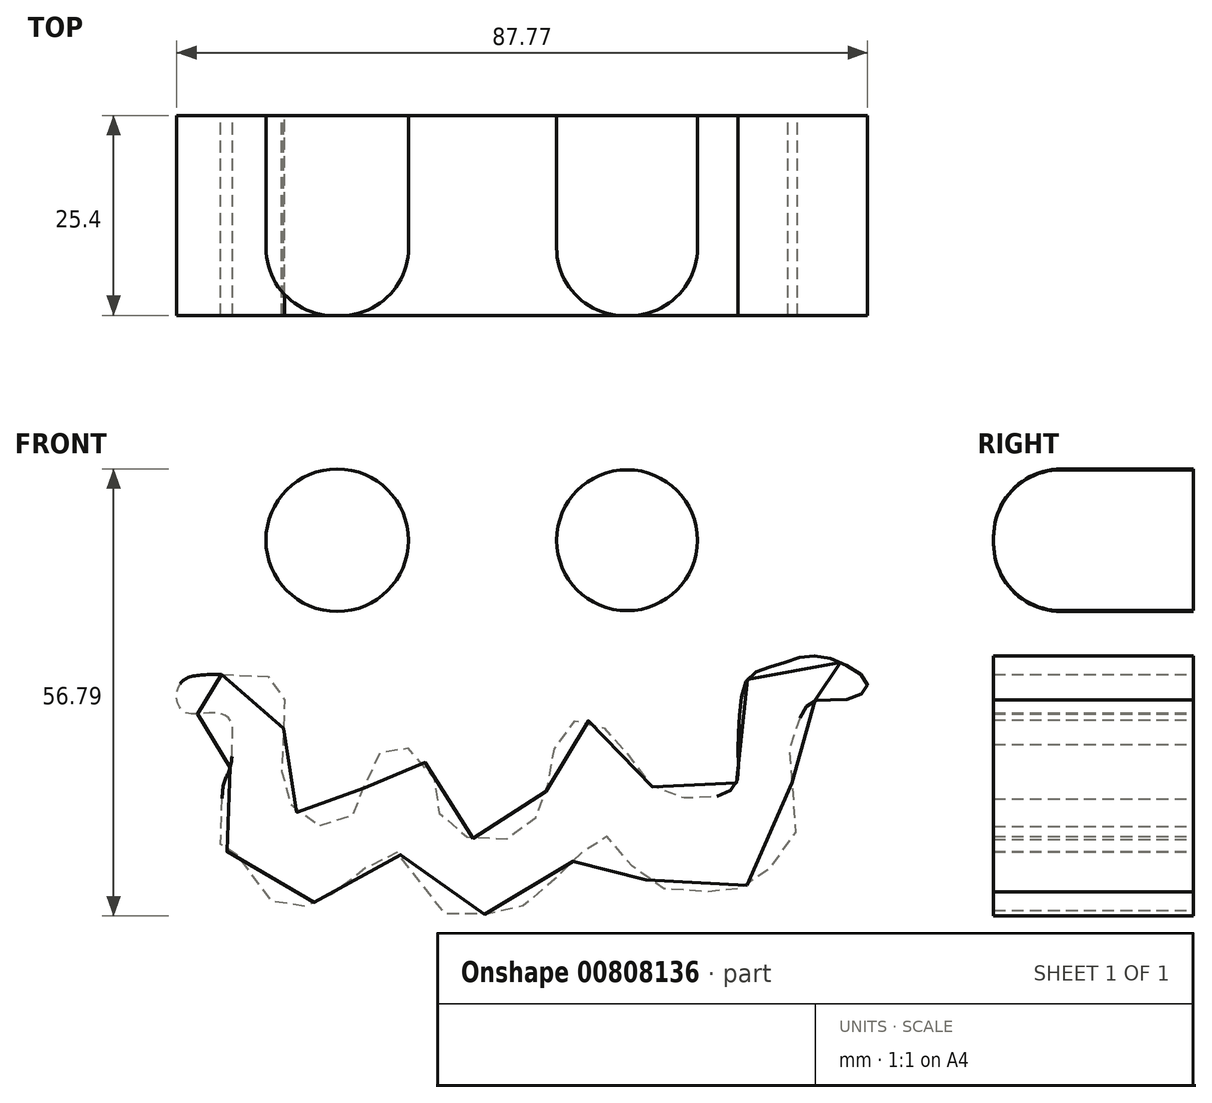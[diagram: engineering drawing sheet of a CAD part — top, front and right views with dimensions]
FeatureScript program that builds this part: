
annotation { "Feature Type Name" : "Feature", "Feature Type Description" : "" }
export const myFeature = defineFeature(function(context is Context, id is Id, definition is map)
    precondition{}
    {
        {
            var Q0;
            Q0=qCreatedBy(makeId("Front.planeOp"),FACE);
            var sketch = newSketch(context, id + "F0", { "sketchPlane" : qUnion([Q0])});
            skCircle(sketch, "E0", {"center": v(-44.17, 39.56) * mm, "radius": 9.05 * mm});
            skCircle(sketch, "E1", {"center": v(-7.34, 39.56) * mm, "radius": 8.95 * mm});
            skFitSpline(sketch, "E2", {"points": [v(-58.86, 22.52) * mm, v(-52.59, 22.13) * mm, v(-51.02, 20.57) * mm, v(-51.02, 15.08) * mm, v(-51.02, 12.14) * mm, v(-51.22, 9.2) * mm, v(-49.85, 5.68) * mm, v(-46.71, 3.33) * mm, v(-42.8, 4.11) * mm, v(-41.03, 6.86) * mm, v(-40.05, 10.38) * mm, v(-37.9, 13.32) * mm, v(-35.55, 13.32) * mm, v(-32.02, 9.8) * mm, v(-31.63, 6.27) * mm, v(-29.28, 2.55) * mm, v(-25.17, 1.57) * mm, v(-20.47, 2.35) * mm, v(-18.31, 5.88) * mm, v(-17.33, 8.81) * mm, v(-16.55, 13.12) * mm, v(-14.4, 16.45) * mm, v(-11.65, 16.45) * mm, v(-9.1, 14.69) * mm, v(-6.56, 11.36) * mm, v(-3.82, 8.03) * mm, v(0, 6.86) * mm, v(3.23, 6.86) * mm, v(6.37, 8.42) * mm, v(6.76, 11.95) * mm, v(6.95, 17.24) * mm, v(8.13, 22.13) * mm, v(11.65, 23.7) * mm, v(15.77, 24.87) * mm, v(20.47, 23.7) * mm, v(23.2, 21.15) * mm, v(20.86, 19.4) * mm, v(16.55, 19.2) * mm, v(14.79, 17.43) * mm, v(13.42, 13.71) * mm, v(13.22, 10.38) * mm, v(14.2, 3.13) * mm, v(10.28, -2.55) * mm, v(6.95, -4.7) * mm, v(3.43, -5.1) * mm, v(-2.64, -4.7) * mm, v(-6.76, -1.76) * mm, v(-10.09, 1.96) * mm, v(-13.02, 0) * mm, v(-15.96, -2.94) * mm, v(-20.47, -6.86) * mm, v(-24.38, -7.83) * mm, v(-30.65, -7.83) * mm, v(-33, -4.7) * mm, v(-36.92, 0) * mm, v(-40.84, -2.35) * mm, v(-45.34, -5.68) * mm, v(-48.08, -6.86) * mm, v(-51.6, -7.05) * mm, v(-57.49, 0) * mm, v(-58.66, 0) * mm, v(-58.86, 5.68) * mm, v(-58.47, 9) * mm, v(-57.68, 10.97) * mm, v(-57.49, 14.89) * mm, v(-57.68, 16.65) * mm, v(-59.64, 17.63) * mm, v(-63.36, 17.63) * mm, v(-64.54, 19.4) * mm, v(-63.75, 21.74) * mm, v(-58.86, 22.52) * mm]});
            skSolve(sketch);
        }
        {
            var Q0;
            Q0=makeQuery(id+"F0.imprint","IMPRINT",FACE,{"disambiguationData":[TD([[makeQuery(id+"F0.imprint","IMPRINT",EDGE,{"derivedFrom":sQuery(id+"F0.wireOp",EDGE,"E2")}),-1.0]])]});
            var Q1;
            Q1=makeQuery(id+"F0.imprint","IMPRINT",FACE,{"disambiguationData":[TD([[makeQuery(id+"F0.imprint","IMPRINT",EDGE,{"derivedFrom":sQuery(id+"F0.wireOp",EDGE,"E0")}),1.0]])]});
            var Q2;
            Q2=makeQuery(id+"F0.imprint","IMPRINT",FACE,{"disambiguationData":[TD([[makeQuery(id+"F0.imprint","IMPRINT",EDGE,{"derivedFrom":sQuery(id+"F0.wireOp",EDGE,"E1")}),1.0]])]});
            extrude(context, id + "F1", {"entities" : qUnion([Q0, Q1, Q2]), "depth" : 25.4 * mm, "offsetDistance" : 25.4 * mm});
        }
        {
            var Q0;
            Q0=makeQuery(id+"F1.opExtrude","CAP_EDGE",EDGE,{"disambiguationData":[OSD([sQuery(id+"F0.wireOp",EDGE,"E0")])],"isStart":false});
            var Q1;
            Q1=makeQuery(id+"F1.opExtrude","CAP_EDGE",EDGE,{"disambiguationData":[OSD([sQuery(id+"F0.wireOp",EDGE,"E1")])],"isStart":false});
            fillet(context, id + "F2", {"entities" : qUnion([Q0, Q1]), "radius" : 8.58 * mm, "tangentPropagation" : true, "allowEdgeOverflow" : false});
        }
    });
